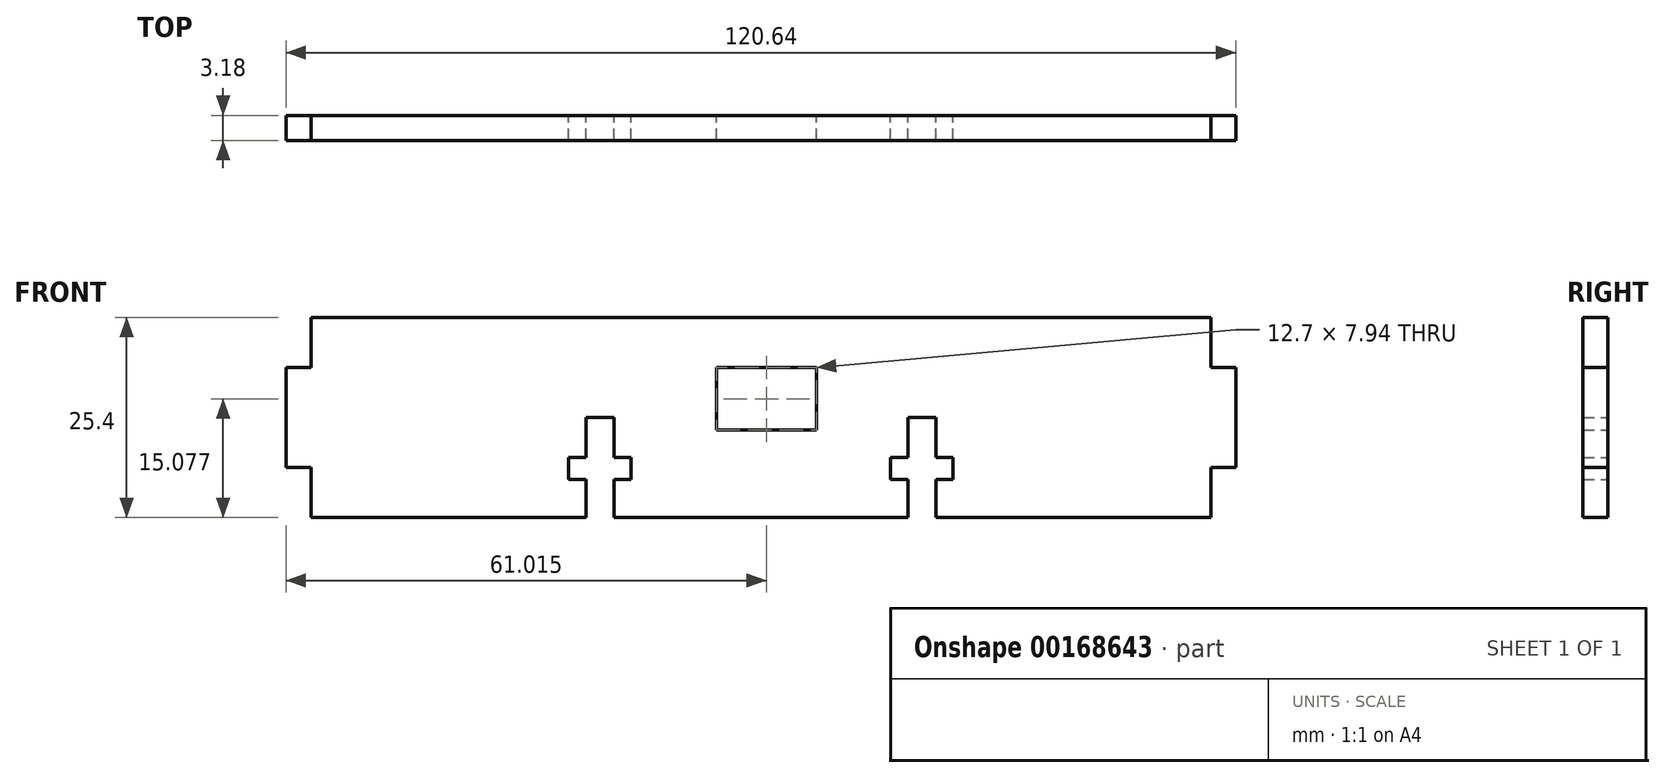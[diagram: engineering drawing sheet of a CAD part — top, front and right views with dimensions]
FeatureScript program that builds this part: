
annotation { "Feature Type Name" : "Feature", "Feature Type Description" : "" }
export const myFeature = defineFeature(function(context is Context, id is Id, definition is map)
    precondition{}
    {
        {
            var Q0;
            Q0=qCreatedBy(makeId("Front.planeOp"),FACE);
            var sketch = newSketch(context, id + "F0", { "sketchPlane" : qUnion([Q0])});
            skLineSegment(sketch, "E0.bottom", {"start": v(-57.15, -5.8) * mm, "end": v(57.15, -5.8) * mm});
            skLineSegment(sketch, "E0.top", {"start": v(-57.15, -31.2) * mm, "end": v(-22.23, -31.2) * mm});
            skLineSegment(sketch, "E0.left", {"start": v(-60.33, -12.14) * mm, "end": v(-60.32, -24.84) * mm});
            skLineSegment(sketch, "E0.right", {"start": v(60.33, -12.14) * mm, "end": v(60.33, -24.84) * mm});
            skLineSegment(sketch, "E1", {"start": v(-60.33, -12.14) * mm, "end": v(-57.15, -12.14) * mm});
            skLineSegment(sketch, "E2", {"start": v(-57.15, -12.14) * mm, "end": v(-57.15, -5.8) * mm});
            skLineSegment(sketch, "E3", {"start": v(-60.32, -24.84) * mm, "end": v(-57.15, -24.84) * mm});
            skLineSegment(sketch, "E4", {"start": v(-57.15, -24.84) * mm, "end": v(-57.15, -31.2) * mm});
            skLineSegment(sketch, "E5.bottom", {"start": v(60.33, -24.84) * mm, "end": v(57.15, -24.84) * mm});
            skLineSegment(sketch, "E5.right", {"start": v(57.15, -24.84) * mm, "end": v(57.15, -31.2) * mm});
            skLineSegment(sketch, "E6.top", {"start": v(60.33, -12.14) * mm, "end": v(57.15, -12.14) * mm});
            skLineSegment(sketch, "E6.right", {"start": v(57.15, -5.8) * mm, "end": v(57.15, -12.14) * mm});
            skLineSegment(sketch, "E7", {"start": v(-22.23, -31.2) * mm, "end": v(-22.23, -26.35) * mm});
            skLineSegment(sketch, "E8", {"start": v(-22.23, -26.35) * mm, "end": v(-24.42, -26.35) * mm});
            skLineSegment(sketch, "E9", {"start": v(-24.42, -26.35) * mm, "end": v(-24.42, -23.57) * mm});
            skLineSegment(sketch, "E10", {"start": v(-24.42, -23.57) * mm, "end": v(-22.23, -23.57) * mm});
            skLineSegment(sketch, "E11", {"start": v(-22.23, -23.57) * mm, "end": v(-22.23, -18.5) * mm});
            skLineSegment(sketch, "E12", {"start": v(-22.23, -18.5) * mm, "end": v(-18.67, -18.5) * mm});
            skLineSegment(sketch, "E13", {"start": v(-18.67, -18.5) * mm, "end": v(-18.67, -23.57) * mm});
            skLineSegment(sketch, "E14", {"start": v(-18.67, -23.57) * mm, "end": v(-16.48, -23.57) * mm});
            skLineSegment(sketch, "E15", {"start": v(-16.48, -23.57) * mm, "end": v(-16.48, -26.35) * mm});
            skLineSegment(sketch, "E16", {"start": v(-16.48, -26.35) * mm, "end": v(-18.67, -26.35) * mm});
            skLineSegment(sketch, "E17", {"start": v(-18.67, -26.35) * mm, "end": v(-18.67, -31.2) * mm});
            skLineSegment(sketch, "E18.MirrorCS", {"start": v(22.23, -18.5) * mm, "end": v(18.67, -18.5) * mm});
            skLineSegment(sketch, "E19.MirrorCS", {"start": v(16.48, -23.57) * mm, "end": v(16.48, -26.35) * mm});
            skLineSegment(sketch, "E20.MirrorCS", {"start": v(18.67, -23.57) * mm, "end": v(16.48, -23.57) * mm});
            skLineSegment(sketch, "E21.MirrorCS", {"start": v(24.42, -23.57) * mm, "end": v(22.23, -23.57) * mm});
            skLineSegment(sketch, "E22.MirrorCS", {"start": v(22.23, -26.35) * mm, "end": v(24.42, -26.35) * mm});
            skLineSegment(sketch, "E23.MirrorCS", {"start": v(16.48, -26.35) * mm, "end": v(18.67, -26.35) * mm});
            skLineSegment(sketch, "E24.MirrorCS", {"start": v(24.42, -26.35) * mm, "end": v(24.42, -23.57) * mm});
            skLineSegment(sketch, "E25.MirrorCS", {"start": v(22.23, -23.57) * mm, "end": v(22.23, -18.5) * mm});
            skLineSegment(sketch, "E26.MirrorCS", {"start": v(18.67, -18.5) * mm, "end": v(18.67, -23.57) * mm});
            skLineSegment(sketch, "E27.MirrorCS", {"start": v(18.67, -26.35) * mm, "end": v(18.67, -31.2) * mm});
            skLineSegment(sketch, "E28.MirrorCS", {"start": v(22.23, -31.2) * mm, "end": v(22.23, -26.35) * mm});
            skLineSegment(sketch, "E29.trimOffspring", {"start": v(-18.67, -31.2) * mm, "end": v(18.67, -31.2) * mm});
            skLineSegment(sketch, "E30.trimOffspring", {"start": v(22.23, -31.2) * mm, "end": v(57.15, -31.2) * mm});
            skLineSegment(sketch, "E31.bottom", {"start": v(-5.65, -12.14) * mm, "end": v(7.05, -12.14) * mm});
            skLineSegment(sketch, "E31.top", {"start": v(-5.65, -20.08) * mm, "end": v(7.05, -20.08) * mm});
            skLineSegment(sketch, "E31.left", {"start": v(-5.65, -12.14) * mm, "end": v(-5.65, -20.08) * mm});
            skLineSegment(sketch, "E31.right", {"start": v(7.05, -12.14) * mm, "end": v(7.05, -20.08) * mm});
            skSolve(sketch);
        }
        {
            var Q0;
            Q0 = qSketchRegion(id + "F0", true);
            extrude(context, id + "F1", {"entities" : qUnion([Q0]), "endBound" : BoundingType.SYMMETRIC, "depth" : 3.17 * mm});
        }
    });
